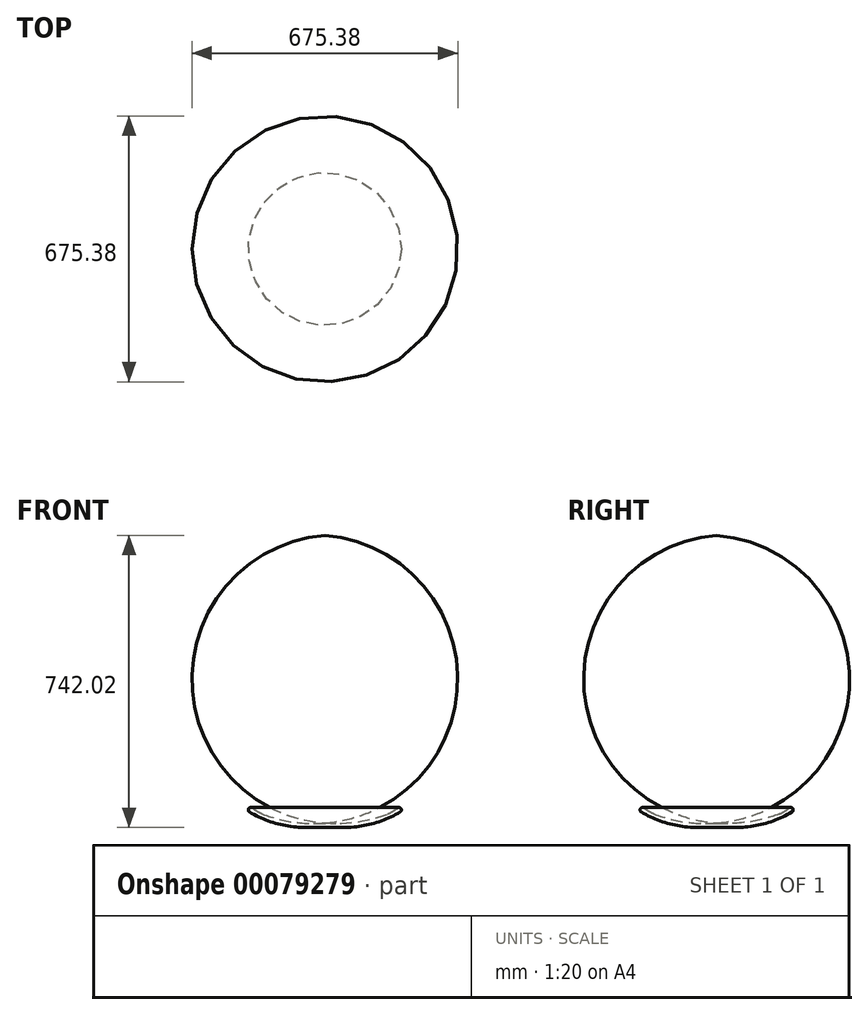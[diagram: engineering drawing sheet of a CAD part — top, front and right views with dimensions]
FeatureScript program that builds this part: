
annotation { "Feature Type Name" : "Feature", "Feature Type Description" : "" }
export const myFeature = defineFeature(function(context is Context, id is Id, definition is map)
    precondition{}
    {
        {
            var Q0;
            Q0=qCreatedBy(makeId("Front.planeOp"),FACE);
            var sketch = newSketch(context, id + "F0", { "sketchPlane" : qUnion([Q0])});
            skLineSegment(sketch, "E0", {"start": v(0, 11.25) * mm, "end": v(0, 0) * mm});
            skLineSegment(sketch, "E1", {"start": v(0, 0) * mm, "end": v(-47.43, 0) * mm});
            skArc(sketch, "E2", {"start": v(-47.43, 0) * mm, "mid": v(-121.94, 9.93) * mm, "end": v(-191.25, 39.04) * mm});
            skArc(sketch, "E3", {"start": v(-191.25, 39.04) * mm, "mid": v(-193.15, 48.29) * mm, "end": v(-183.75, 49.19) * mm});
            skArc(sketch, "E4", {"start": v(-183.75, 49.19) * mm, "mid": v(-172.33, 40.54) * mm, "end": v(-159.49, 34.19) * mm});
            skArc(sketch, "E5", {"start": v(-159.49, 34.19) * mm, "mid": v(-81.02, 13.85) * mm, "end": v(0, 11.25) * mm});
            skSolve(sketch);
        }
        {
            var Q0;
            Q0=makeQuery(id+"F0.imprint","IMPRINT",FACE,{"disambiguationData":[TD([[makeQuery(id+"F0.imprint","IMPRINT",EDGE,{"derivedFrom":sQuery(id+"F0.wireOp",EDGE,"E0")}),-1.0]])]});
            var Q1;
            Q1=sQuery(id+"F0.wireOp",EDGE,"E0");
            revolve(context, id + "F1", {"entities" : qUnion([Q0]), "axis" : qUnion([Q1]), "revolveType" : RevolveType.FULL});
        }
    });
